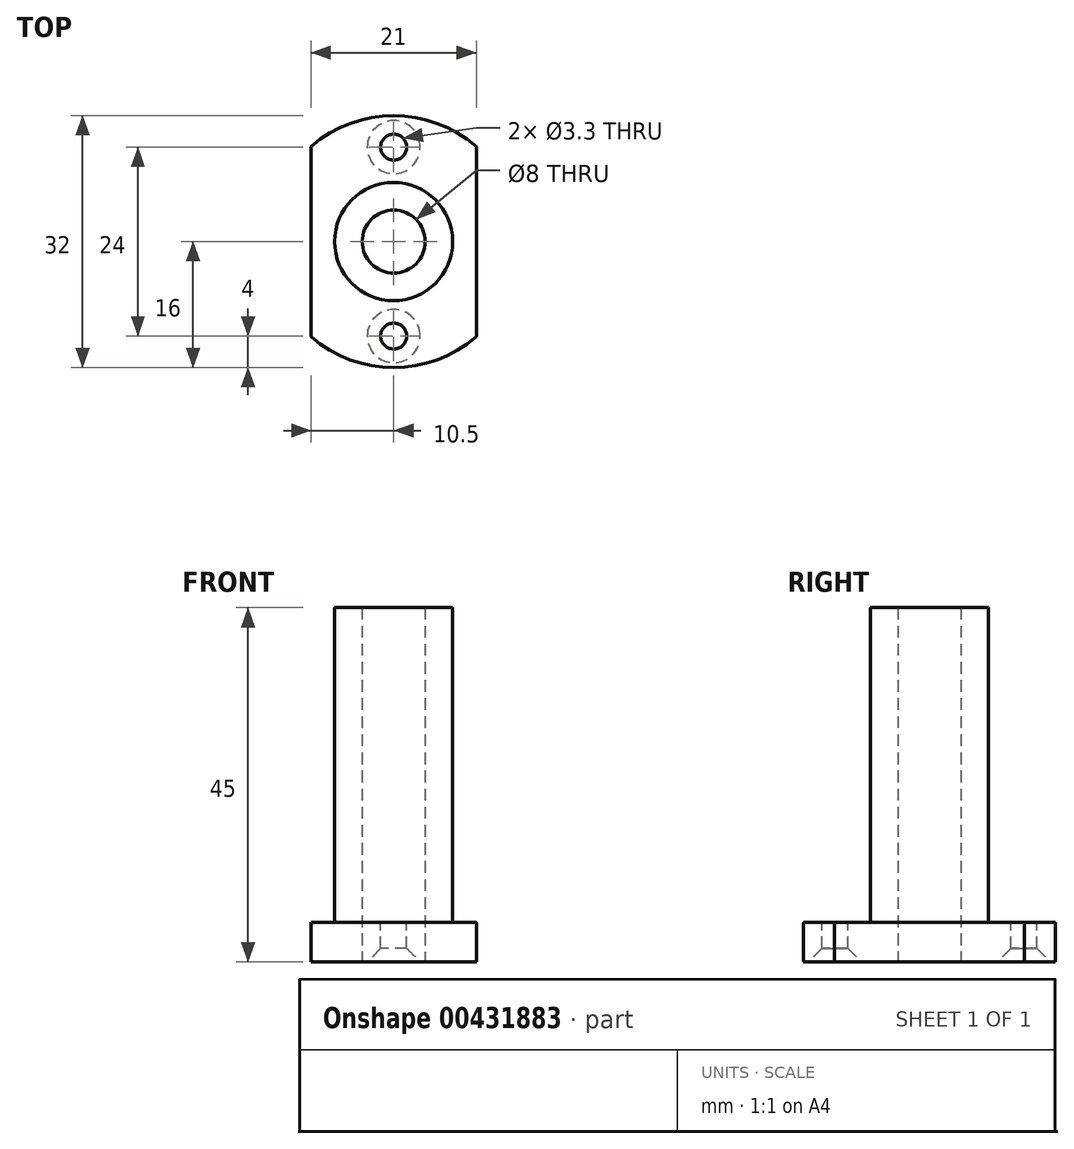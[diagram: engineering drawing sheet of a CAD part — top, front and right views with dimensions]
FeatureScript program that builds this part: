
annotation { "Feature Type Name" : "Feature", "Feature Type Description" : "" }
export const myFeature = defineFeature(function(context is Context, id is Id, definition is map)
    precondition{}
    {
        {
            var Q0;
            Q0=qCreatedBy(makeId("Top.planeOp"),FACE);
            var sketch = newSketch(context, id + "F0", { "sketchPlane" : qUnion([Q0])});
            skLineSegment(sketch, "E0", {"start": v(-10.5, 12.07) * mm, "end": v(-10.5, -12.07) * mm});
            skLineSegment(sketch, "E1", {"start": v(10.5, 12.07) * mm, "end": v(10.5, -12.07) * mm});
            skArc(sketch, "E2", {"start": v(10.5, 12.07) * mm, "mid": v(0, 16) * mm, "end": v(-10.5, 12.07) * mm});
            skArc(sketch, "E3", {"start": v(-10.5, -12.07) * mm, "mid": v(0, -16) * mm, "end": v(10.5, -12.07) * mm});
            skPoint(sketch, "E4", {"position": v(0, 12) * mm});
            skPoint(sketch, "E5", {"position": v(0, -12) * mm});
            skCircle(sketch, "E6", {"center": v(0, 0) * mm, "radius": 4 * mm});
            skSolve(sketch);
        }
        {
            var Q0;
            Q0=makeQuery(id+"F0.imprint","IMPRINT",FACE,{"disambiguationData":[TD([[makeQuery(id+"F0.imprint","IMPRINT",EDGE,{"derivedFrom":sQuery(id+"F0.wireOp",EDGE,"E0")}),1.0]])]});
            extrude(context, id + "F1", {"entities" : qUnion([Q0]), "depth" : 5 * mm, "offsetDistance" : 25 * mm});
        }
        {
            var Q0;
            Q0=sQuery(id+"F0.wireOp",VERTEX,"E4");
            var Q1;
            Q1=sQuery(id+"F0.wireOp",VERTEX,"E5");
            var Q2;
            Q2=makeQuery(id+"F1.opExtrude","SWEPT_BODY",BODY,{"disambiguationData":[OSD([sQuery(id+"F0.wireOp",EDGE,"E0"),sQuery(id+"F0.wireOp",EDGE,"E1"),sQuery(id+"F0.wireOp",EDGE,"E2"),sQuery(id+"F0.wireOp",EDGE,"E3"),sQuery(id+"F0.wireOp",EDGE,"E6")])]});
            hole(context, id + "F2", {"style" : HoleStyle.C_SINK, "endStyle" : HoleEndStyle.BLIND, "oppositeDirection" : true, "standardTappedOrClearance" : lookupTablePath({ "standard" : "ISO", "fit" : "Normal", "size" : "M3", "type" : "Clearance" }), "standardBlindInLast" : lookupTablePath({ "fit" : "Standard", "standard" : "ISO", "size" : "M3", "type" : "Clearance" }), "holeDiameter" : 3.3 * mm, "cSinkDiameter" : 6.72 * mm, "cSinkAngle" : 90 * degree, "majorDiameter" : 5 * mm, "holeDepth" : 10 * mm, "isTappedThrough" : true, "tappedDepth" : 12 * mm, "tapClearance" : 3, "locations" : qUnion([Q0, Q1]), "scope" : qUnion([Q2]), "startStyle" : HoleStartStyle.PART});
        }
        {
            var Q0;
            Q0=makeQuery(id+"F1.opExtrude","CAP_FACE",FACE,{"disambiguationData":[OSD([sQuery(id+"F0.wireOp",EDGE,"E0"),sQuery(id+"F0.wireOp",EDGE,"E1"),sQuery(id+"F0.wireOp",EDGE,"E2"),sQuery(id+"F0.wireOp",EDGE,"E3"),sQuery(id+"F0.wireOp",EDGE,"E6")])],"isStart":false});
            var sketch = newSketch(context, id + "F3", { "sketchPlane" : qUnion([Q0])});
            skCircle(sketch, "E7", {"center": v(0, 0) * mm, "radius": 7.5 * mm});
            skSolve(sketch);
        }
        {
            var Q0;
            Q0=makeQuery(id+"F3.imprint","IMPRINT",FACE,{"disambiguationData":[TD([[makeQuery(id+"F3.imprint","IMPRINT",EDGE,{"derivedFrom":sQuery(id+"F3.wireOp",EDGE,"E7")}),1.0]])]});
            extrude(context, id + "F4", {"entities" : qUnion([Q0]), "operationType" : NewBodyOperationType.ADD, "depth" : 40 * mm, "offsetDistance" : 25 * mm});
        }
    });
